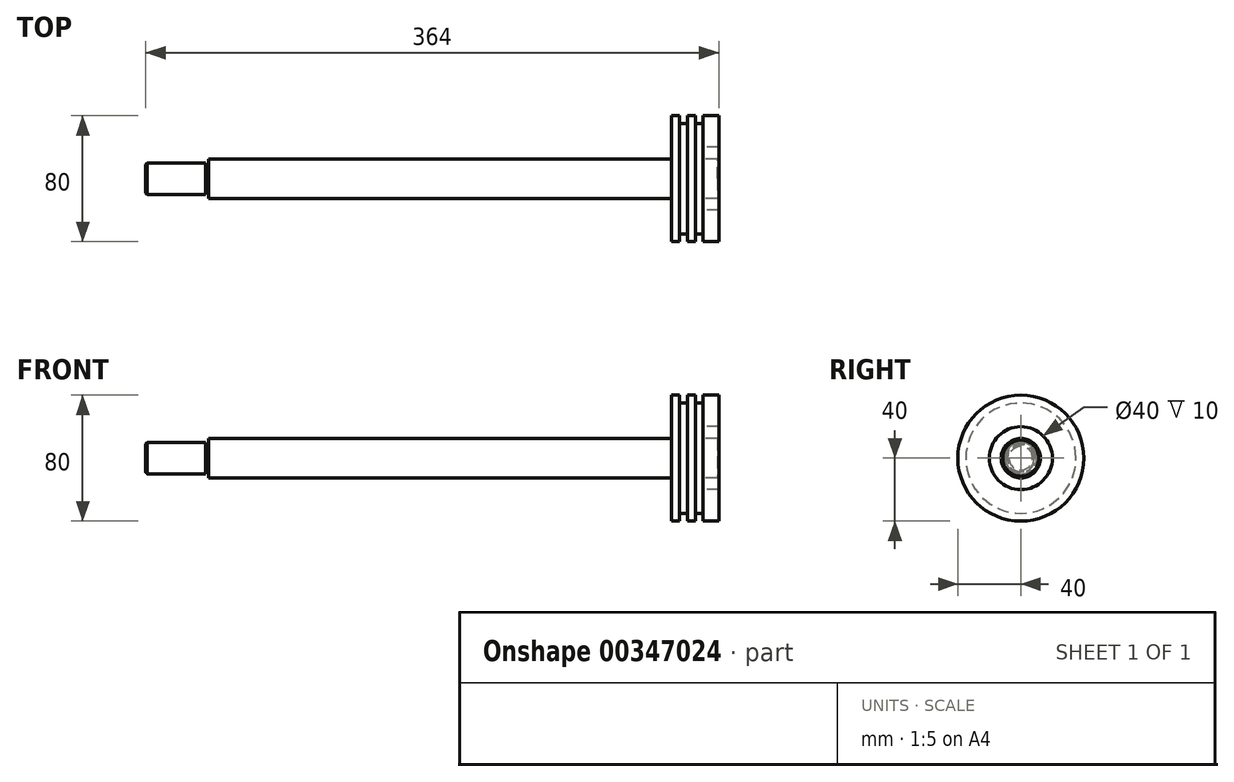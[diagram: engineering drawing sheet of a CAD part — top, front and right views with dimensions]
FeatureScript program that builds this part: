
annotation { "Feature Type Name" : "Feature", "Feature Type Description" : "" }
export const myFeature = defineFeature(function(context is Context, id is Id, definition is map)
    precondition{}
    {
        {
            var Q0;
            Q0=qCreatedBy(makeId("Front.planeOp"),FACE);
            var sketch = newSketch(context, id + "F0", { "sketchPlane" : qUnion([Q0])});
            skLineSegment(sketch, "E0.0", {"start": v(0, 12.5) * mm, "end": v(294, 12.5) * mm});
            skLineSegment(sketch, "E1", {"start": v(0, 7.5) * mm, "end": v(0, 12.5) * mm});
            skLineSegment(sketch, "E2", {"start": v(324, 12.5) * mm, "end": v(324, 0) * mm});
            skLineSegment(sketch, "E3.0", {"start": v(294, 40) * mm, "end": v(299, 40) * mm});
            skLineSegment(sketch, "E4.0", {"start": v(314, 12.5) * mm, "end": v(314, 20) * mm});
            skLineSegment(sketch, "E5.0", {"start": v(309, 35) * mm, "end": v(309, 40) * mm});
            skLineSegment(sketch, "E6.0", {"start": v(304, 35) * mm, "end": v(304, 40) * mm});
            skLineSegment(sketch, "E7.0", {"start": v(299, 35) * mm, "end": v(299, 40) * mm});
            skLineSegment(sketch, "E8.2", {"start": v(299, 35) * mm, "end": v(304, 35) * mm});
            skLineSegment(sketch, "E9.trimOffspring", {"start": v(314, 40) * mm, "end": v(324, 40) * mm});
            skLineSegment(sketch, "E10.trimOffspring", {"start": v(304, 40) * mm, "end": v(309, 40) * mm});
            skLineSegment(sketch, "E11.0", {"start": v(294, 12.5) * mm, "end": v(294, 40) * mm});
            skLineSegment(sketch, "E12.trimOffspring", {"start": v(314, 35) * mm, "end": v(314, 40) * mm});
            skLineSegment(sketch, "E13.trimOffspring", {"start": v(309, 35) * mm, "end": v(314, 35) * mm});
            skLineSegment(sketch, "E14.trimOffspring", {"start": v(314, 12.5) * mm, "end": v(324, 12.5) * mm});
            skLineSegment(sketch, "E15.0", {"start": v(-2, 7.5) * mm, "end": v(0, 7.5) * mm});
            skLineSegment(sketch, "E16.0", {"start": v(-2, 7.5) * mm, "end": v(-2, 10) * mm});
            skLineSegment(sketch, "E17.trimOffspring", {"start": v(0, 7.5) * mm, "end": v(0, 73.4) * mm, "construction": true});
            skLineSegment(sketch, "E18.0", {"start": v(-2, 10) * mm, "end": v(-40, 10) * mm});
            skLineSegment(sketch, "E19", {"start": v(-40, 10) * mm, "end": v(-40, 0) * mm});
            skLineSegment(sketch, "E20", {"start": v(-40, 0) * mm, "end": v(324, 0) * mm});
            skLineSegment(sketch, "E21", {"start": v(324, 40) * mm, "end": v(324, 20) * mm});
            skLineSegment(sketch, "E22", {"start": v(324, 20) * mm, "end": v(314, 20) * mm});
            skSolve(sketch);
        }
        {
            var Q0;
            Q0=makeQuery(id+"F0.imprint","IMPRINT",FACE,{"disambiguationData":[TD([[makeQuery(id+"F0.imprint","IMPRINT",EDGE,{"derivedFrom":sQuery(id+"F0.wireOp",EDGE,"E0.0")}),-1.0]])]});
            var Q1;
            Q1=sQuery(id+"F0.wireOp",EDGE,"E20");
            revolve(context, id + "F1", {"entities" : qUnion([Q0]), "axis" : qUnion([Q1]), "revolveType" : RevolveType.FULL});
        }
        {
            var Q0;
            Q0=makeQuery(id+"F1.opRevolve","SWEPT_EDGE",EDGE,{"disambiguationData":[OSD([sQuery(id+"F0.wireOp",EDGE,"E15.0"),sQuery(id+"F0.wireOp",EDGE,"E16.0")])]});
            var Q1;
            Q1=makeQuery(id+"F1.opRevolve","SWEPT_EDGE",EDGE,{"disambiguationData":[OSD([sQuery(id+"F0.wireOp",EDGE,"E18.0"),sQuery(id+"F0.wireOp",EDGE,"E19")])]});
            chamfer(context, id + "F2", {"entities" : qUnion([Q0, Q1]), "width" : 1 * mm, "tangentPropagation" : true});
        }
        {
            var Q0;
            Q0=makeQuery(id+"F1.opRevolve","SWEPT_EDGE",EDGE,{"disambiguationData":[OSD([sQuery(id+"F0.wireOp",EDGE,"E2"),sQuery(id+"F0.wireOp",EDGE,"E14.trimOffspring")])]});
            var Q1;
            Q1=makeQuery(id+"F1.opRevolve","SWEPT_EDGE",EDGE,{"disambiguationData":[OSD([sQuery(id+"F0.wireOp",EDGE,"RXzYf0xF-ZaW4-j8hk-B8iR-eg3UiJspn1rt"),sQuery(id+"F0.wireOp",EDGE,"1edb6dcb-366a-45e7-8591-0f7d55113d93.trimOffspring")])]});
            chamfer(context, id + "F3", {"entities" : qUnion([Q0, Q1]), "width" : 1 * mm, "tangentPropagation" : true});
        }
    });
